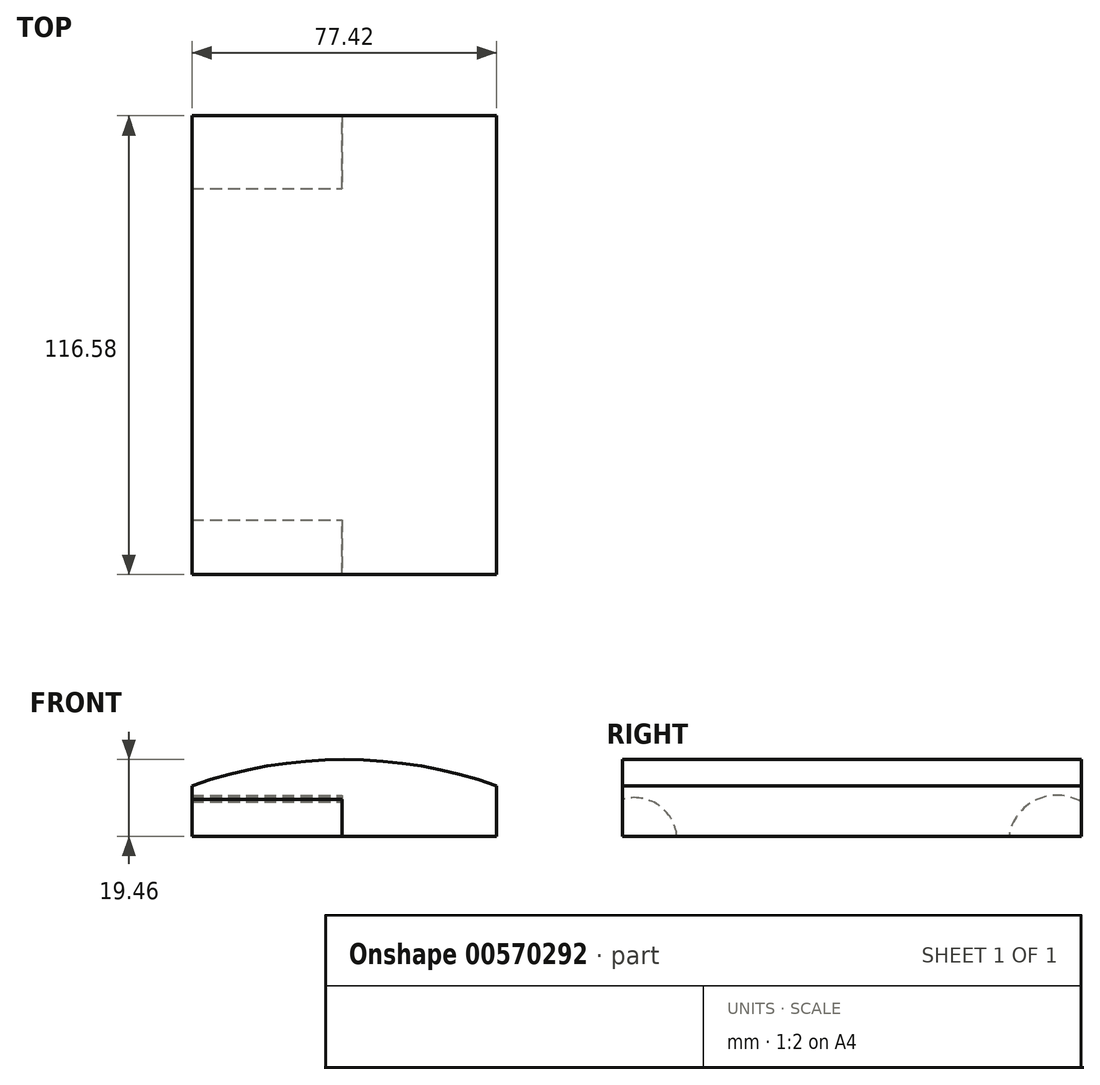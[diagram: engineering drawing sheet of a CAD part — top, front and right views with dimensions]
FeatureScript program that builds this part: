
annotation { "Feature Type Name" : "Feature", "Feature Type Description" : "" }
export const myFeature = defineFeature(function(context is Context, id is Id, definition is map)
    precondition{}
    {
        {
            var Q0;
            Q0=qCreatedBy(makeId("Front.planeOp"),FACE);
            var sketch = newSketch(context, id + "F0", { "sketchPlane" : qUnion([Q0])});
            skLineSegment(sketch, "E0.bottom", {"start": v(-38.13, 0) * mm, "end": v(39.29, 0) * mm});
            skLineSegment(sketch, "E0.top", {"start": v(-38.13, -12.8) * mm, "end": v(39.29, -12.8) * mm});
            skLineSegment(sketch, "E0.left", {"start": v(-38.13, 0) * mm, "end": v(-38.13, -12.8) * mm});
            skLineSegment(sketch, "E0.right", {"start": v(39.29, 0) * mm, "end": v(39.29, -12.8) * mm});
            skArc(sketch, "E1", {"start": v(39.29, 0) * mm, "mid": v(0.58, 6.65) * mm, "end": v(-38.13, 0) * mm});
            skSolve(sketch);
        }
        {
            var Q0;
            Q0=makeQuery(id+"F0.imprint","IMPRINT",FACE,{"disambiguationData":[TD([[makeQuery(id+"F0.imprint","IMPRINT",EDGE,{"derivedFrom":sQuery(id+"F0.wireOp",EDGE,"E0.bottom")}),-1.0]])]});
            var Q1;
            Q1=makeQuery(id+"F0.imprint","IMPRINT",FACE,{"disambiguationData":[TD([[makeQuery(id+"F0.imprint","IMPRINT",EDGE,{"derivedFrom":sQuery(id+"F0.wireOp",EDGE,"E0.bottom")}),1.0]])]});
            extrude(context, id + "F1", {"entities" : qUnion([Q0, Q1]), "depth" : 63 * mm, "offsetDistance" : 25.4 * mm, "hasSecondDirection" : true, "secondDirectionOppositeDirection" : true, "secondDirectionDepth" : 53.6 * mm});
        }
        {
            var Q0;
            Q0=qCreatedBy(makeId("Right.planeOp"),FACE);
            var sketch = newSketch(context, id + "F2", { "sketchPlane" : qUnion([Q0])});
            skCircle(sketch, "E2", {"center": v(-60.04, -13.96) * mm, "radius": 10.93 * mm});
            skCircle(sketch, "E3", {"center": v(47.3, -14.82) * mm, "radius": 12.38 * mm});
            skSolve(sketch);
        }
        {
            var Q0;
            Q0 = qSketchRegion(id + "F2", true);
            extrude(context, id + "F3", {"entities" : qUnion([Q0]), "operationType" : NewBodyOperationType.REMOVE, "oppositeDirection" : true, "depth" : 47 * mm, "offsetDistance" : 25.4 * mm});
        }
    });
